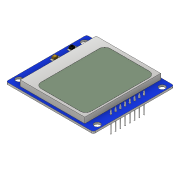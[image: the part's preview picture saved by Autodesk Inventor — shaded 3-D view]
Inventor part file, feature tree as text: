
AUTODESK INVENTOR PART (.ipt)
format: ipt  version: 2019 (Build 230136000, 136)  size: 326,144 bytes
history: native  units: in
note: dims shown in document units (in); Inventor stores cm internally (conversion verified against a paired STEP export)
features: extrude x9, sketch x9, draft x8, pattern_linear x3, fillet x3, projected_geometry x1
ambient origin geometry x8: Origin, YZ Plane, XZ Plane, XY Plane, X Axis, Y Axis, Z Axis, Center Point
bodies: Solid1 (feature_tree)
feature tree (33):
  extrude  "Extrusion1"  Depth=1.6732in
  extrude  "Extrusion2"  Depth=1.3386in
  extrude  "Extrusion3"  Depth=0.1181in TaperAngle=0.0deg
  extrude  "Extrusion4"  Depth=0.2362in
  extrude  "Extrusion5"  Depth=1.437in
  pattern_linear  "Rectangular Pattern1"  Spacing1=0.0906in  [1 undecoded]
  fillet  "Fillet1"  Radius=0.126in
  fillet  "Fillet2"  Radius=0.1535in
  extrude  "Extrusion6"  Depth=0.1969in
  extrude  "Extrusion7"  Depth=0.1969in
  fillet  "Fillet3"  Radius=0.0945in
  extrude  "Extrusion8"  Depth=0.1969in
  pattern_linear  "Rectangular Pattern2"  Spacing1=0.126in  [1 undecoded]
  extrude  "Extrusion9"  Depth=0.1969in
  pattern_linear  "Rectangular Pattern3"  Spacing1=0.0906in  [1 undecoded]
  draft  "FaceDraft1"
  draft  "FaceDraft2"
  draft  "FaceDraft3"
  draft  "FaceDraft4"
  draft  "FaceDraft5"
  draft  "FaceDraft6"
  draft  "FaceDraft7"
  draft  "FaceDraft8"
  sketch  "Sketch1"  dims[d0=1.811in d1=1.6732in]
  sketch  "Sketch2"  dims[d2=0.0394in d3=0.0in d4=1.3386in]
  sketch  "Sketch3"  dims[d5=1.5748in d6=0.1181in d7=0.0in]
  sketch  "Sketch4"  dims[d8=0.2362in d9=0.2362in]
  sketch  "Sketch5"  dims[d10=1.0433in d11=1.437in]
  sketch  "Sketch7"  dims[d13=0.0394in]
  sketch  "Sketch8"  dims[d14=0.002in d15=0.0in]
  sketch  "Sketch9"  dims[d16=0.126in]
  projected_geometry  "Projected Loop2"
  sketch  "Sketch10"  dims[d17=0.1535in d18=0.0906in d19=0.126in d20=0.1535in d21=0.1063in d22=0.126in d23=0.0945in d24=0.1732in d25=0.126in d26=0.1732in d27=0.0906in d28=0.0039in d29=0.0in d32=0.0197in d33=0.1378in d34=0.502in d35=0.0039in d36=0.0in d37=3.1496in d39=0.0984in d43=0.0394in d44=0.1181in d45=0.0591in d46=0.1575in d47=0.002in d48=0.0in d49=0.1181in d50=0.8268in d51=0.0591in d52=0.4724in d53=0.0787in d54=0.0394in d55=0.0394in d56=0.0787in d57=0.0394in d58=0.0394in d59=0.0in d60=0.0098in d61=0.0984in d63=0.0787in d64=0.0in d65=3.1496in d67=0.0984in d68=0.0197in d69=0.2362in d70=0.0in d71=0.1969in d72=0.0in d73=3.1496in d75=0.0984in d76=0.0344in d77=0.0344in d78=0.0344in d79=0.0344in d80=0.0344in d81=0.0344in d82=0.0344in d83=0.0344in]
note: 3 required parameter values undecoded (feature->parameter linkage not recoverable at this tier; creation-order binding heuristic only, values carry confidence <= 0.55)
